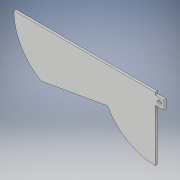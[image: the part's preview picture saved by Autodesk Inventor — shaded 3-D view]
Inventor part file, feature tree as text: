
AUTODESK INVENTOR PART (.ipt)
format: ipt  version: 2019 (Build 230136000, 136)  size: 120,320 bytes
history: native  units: in
note: dims shown in document units (in); Inventor stores cm internally (conversion verified against a paired STEP export)
features: extrude x2, sketch x2
ambient origin geometry x8: Origin, YZ Plane, XZ Plane, XY Plane, X Axis, Y Axis, Z Axis, Center Point
bodies: Solid1 (feature_tree)
feature tree (4):
  extrude  "Extrusion1"  Depth=3.125in
  extrude  "Extrusion2"  Depth=0.125in
  sketch  "Sketch1"  dims[d0=3.125in d1=2.706in]
  sketch  "Sketch2"  dims[d2=1.563in d3=4.0in d4=0.0687in d5=3.125in d6=3.0in d7=0.125in d9=0.0in d10=0.0in d11=1.928in d12=0.125in d13=0.0in d14=0.5in d15=0.5in d16=3.6361in d17=0.25in d18=3.25in d19=0.25in d20=0.125in d21=0.0in]
